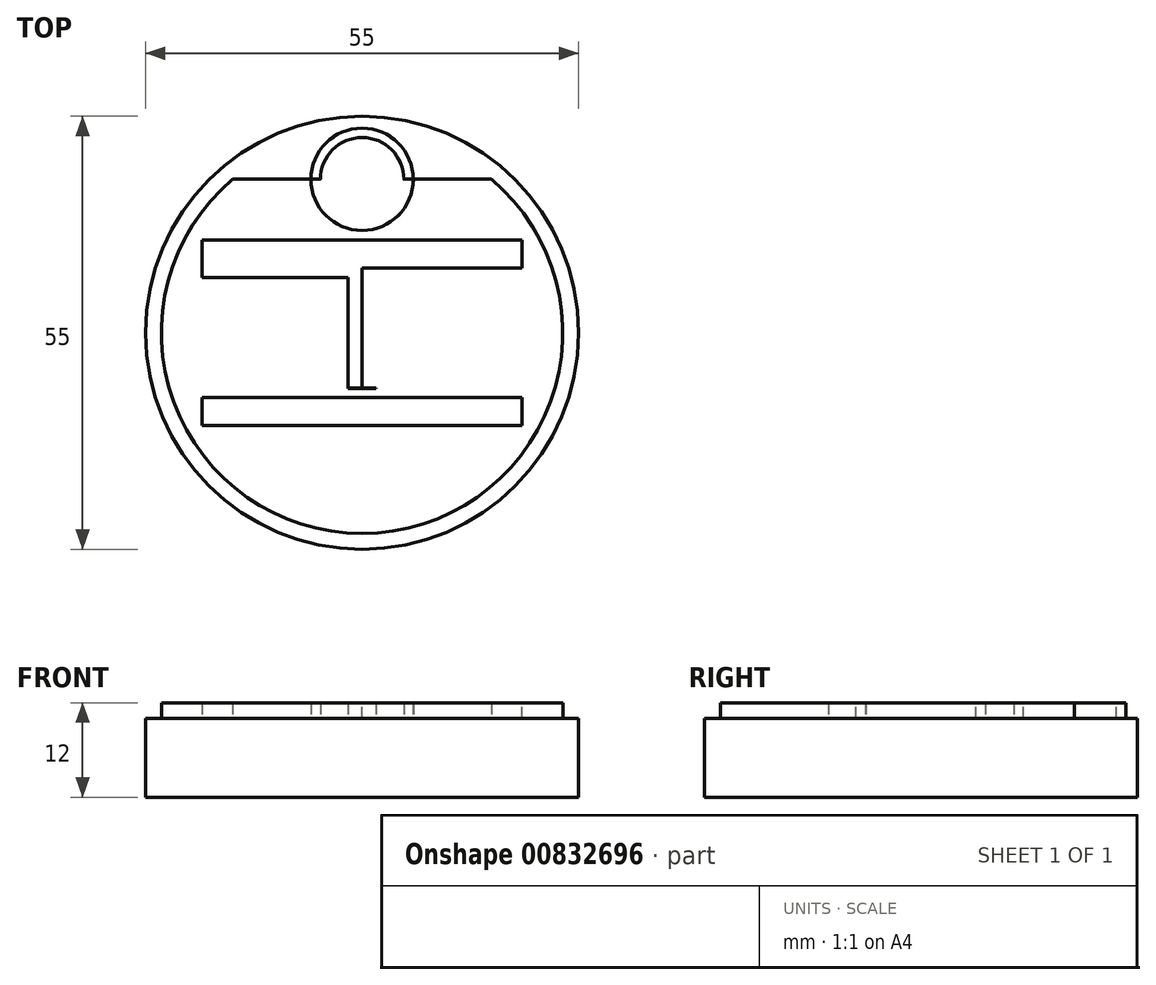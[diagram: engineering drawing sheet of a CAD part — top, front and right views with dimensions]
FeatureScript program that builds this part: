
annotation { "Feature Type Name" : "Feature", "Feature Type Description" : "" }
export const myFeature = defineFeature(function(context is Context, id is Id, definition is map)
    precondition{}
    {
        {
            var Q0;
            Q0=qCreatedBy(makeId("Top.planeOp"),FACE);
            var sketch = newSketch(context, id + "F0", { "sketchPlane" : qUnion([Q0])});
            skCircle(sketch, "E0", {"center": v(0, 0) * mm, "radius": 27.5 * mm});
            skSolve(sketch);
        }
        {
            var Q0;
            Q0=makeQuery(id+"F0.imprint","IMPRINT",FACE,{"disambiguationData":[TD([[makeQuery(id+"F0.imprint","IMPRINT",EDGE,{"derivedFrom":sQuery(id+"F0.wireOp",EDGE,"E0")}),1.0]])]});
            extrude(context, id + "F1", {"entities" : qUnion([Q0]), "depth" : 10 * mm, "offsetDistance" : 25 * mm});
        }
        {
            var Q0;
            Q0=makeQuery(id+"F1.opExtrude","CAP_FACE",FACE,{"disambiguationData":[OSD([sQuery(id+"F0.wireOp",EDGE,"E0")])],"isStart":false});
            var sketch = newSketch(context, id + "F2", { "sketchPlane" : qUnion([Q0])});
            skCircle(sketch, "E1.0", {"center": v(0, 0) * mm, "radius": 25.5 * mm});
            skLineSegment(sketch, "E2.bottom", {"start": v(-3, -7) * mm, "end": v(3, -7) * mm});
            skLineSegment(sketch, "E2.top", {"start": v(-3, 7) * mm, "end": v(3, 7) * mm});
            skLineSegment(sketch, "E2.left", {"start": v(-3, -7) * mm, "end": v(-3, 7) * mm});
            skLineSegment(sketch, "E2.right", {"start": v(3, -7) * mm, "end": v(3, 7) * mm});
            skLineSegment(sketch, "E3.0", {"start": v(-3, -10) * mm, "end": v(3, -10) * mm});
            skLineSegment(sketch, "E4.0", {"start": v(0, -7) * mm, "end": v(0, 12) * mm});
            skLineSegment(sketch, "E5.bottom", {"start": v(21.5, -7.05) * mm, "end": v(-21.5, -7.05) * mm});
            skLineSegment(sketch, "E5.top", {"start": v(21.5, -12.95) * mm, "end": v(-21.5, -12.95) * mm});
            skLineSegment(sketch, "E5.left", {"start": v(21.5, -7.05) * mm, "end": v(21.5, -12.95) * mm});
            skLineSegment(sketch, "E5.right", {"start": v(-21.5, -7.05) * mm, "end": v(-21.5, -12.95) * mm});
            skPoint(sketch, "E5.middle", {"position": v(0, -10) * mm});
            skLineSegment(sketch, "E6.0", {"start": v(-3, 10) * mm, "end": v(3, 10) * mm});
            skLineSegment(sketch, "E7.bottom", {"start": v(21.5, 13) * mm, "end": v(-21.5, 13) * mm});
            skLineSegment(sketch, "E7.top", {"start": v(21.5, 7) * mm, "end": v(-21.5, 7) * mm});
            skLineSegment(sketch, "E7.left", {"start": v(21.5, 13) * mm, "end": v(21.5, 7) * mm});
            skLineSegment(sketch, "E7.right", {"start": v(-21.5, 13) * mm, "end": v(-21.5, 7) * mm});
            skPoint(sketch, "E7.middle", {"position": v(0, 10) * mm});
            skLineSegment(sketch, "E8.0", {"start": v(21.5, 19.5) * mm, "end": v(-21.5, 19.5) * mm});
            skCircle(sketch, "E9", {"center": v(0, 19.5) * mm, "radius": 6.5 * mm});
            skCircle(sketch, "E10", {"center": v(0, 19.5) * mm, "radius": 3.5 * mm});
            skCircle(sketch, "E11.0", {"center": v(0, 19.5) * mm, "radius": 5.3 * mm});
            skLineSegment(sketch, "E12.0", {"start": v(21.5, 11.8) * mm, "end": v(-21.5, 11.8) * mm});
            skLineSegment(sketch, "E13.0", {"start": v(21.5, 8.2) * mm, "end": v(-21.5, 8.2) * mm});
            skLineSegment(sketch, "E14.0", {"start": v(-3, -6) * mm, "end": v(3, -6) * mm});
            skLineSegment(sketch, "E15.0", {"start": v(-3, 6) * mm, "end": v(3, 6) * mm});
            skLineSegment(sketch, "E16.0", {"start": v(21.5, -8.25) * mm, "end": v(-21.5, -8.25) * mm});
            skLineSegment(sketch, "E17.0", {"start": v(21.5, -11.75) * mm, "end": v(-21.5, -11.75) * mm});
            skLineSegment(sketch, "E18.0", {"start": v(1.8, -7) * mm, "end": v(1.8, 7) * mm});
            skLineSegment(sketch, "E19.0", {"start": v(-1.8, -7) * mm, "end": v(-1.8, 7) * mm});
            skLineSegment(sketch, "E20.0", {"start": v(-20.3, -7.05) * mm, "end": v(-20.3, -12.95) * mm});
            skLineSegment(sketch, "E21.0", {"start": v(20.3, -7.05) * mm, "end": v(20.3, -12.95) * mm});
            skLineSegment(sketch, "E22.0", {"start": v(20.3, 13) * mm, "end": v(20.3, 7) * mm});
            skLineSegment(sketch, "E23.0", {"start": v(-20.3, 13) * mm, "end": v(-20.3, 7) * mm});
            skLineSegment(sketch, "E24", {"start": v(-1.8, 7) * mm, "end": v(-1.8, 8.2) * mm});
            skLineSegment(sketch, "E25", {"start": v(-1.8, 8.2) * mm, "end": v(-1.8, 7) * mm});
            skLineSegment(sketch, "E26", {"start": v(1.8, 7) * mm, "end": v(1.8, 8.2) * mm});
            skLineSegment(sketch, "E27", {"start": v(1.8, 8.2) * mm, "end": v(1.8, -7) * mm});
            skLineSegment(sketch, "E28", {"start": v(1.8, -7) * mm, "end": v(1.8, -8.25) * mm});
            skLineSegment(sketch, "E29", {"start": v(1.8, -8.25) * mm, "end": v(1.8, -7) * mm});
            skLineSegment(sketch, "E30", {"start": v(-1.8, -7) * mm, "end": v(-1.8, -8.25) * mm});
            skSolve(sketch);
        }
        {
            var Q0;
            {var subQ0=sQuery(id+"F2.wireOp",EDGE,"E5.left");var subQ1=sQuery(id+"F2.wireOp",EDGE,"E5.bottom");var subQ2=makeQuery(id+"F2.imprint","INTERSECT",VERTEX,{"derivedFrom":[subQ1,subQ0]});Q0=makeQuery(id+"F2.imprint","IMPRINT",FACE,{"disambiguationData":[TD([[makeQuery(id+"F2.imprint","IMPRINT",EDGE,{"disambiguationData":[TD([[subQ2,-1.0]])],"derivedFrom":subQ1}),1.0]])]});}
            var Q1;
            {var subQ0=sQuery(id+"F2.wireOp",EDGE,"E5.right");var subQ1=sQuery(id+"F2.wireOp",EDGE,"E5.bottom");var subQ2=makeQuery(id+"F2.imprint","INTERSECT",VERTEX,{"derivedFrom":[subQ1,subQ0]});Q1=makeQuery(id+"F2.imprint","IMPRINT",FACE,{"disambiguationData":[TD([[makeQuery(id+"F2.imprint","IMPRINT",EDGE,{"disambiguationData":[TD([[subQ2,1.0]])],"derivedFrom":subQ1}),1.0]])]});}
            var Q2;
            {var subQ0=sQuery(id+"F2.wireOp",EDGE,"E21.0");var subQ1=sQuery(id+"F2.wireOp",EDGE,"E5.bottom");var subQ2=makeQuery(id+"F2.imprint","INTERSECT",VERTEX,{"derivedFrom":[subQ1,subQ0]});Q2=makeQuery(id+"F2.imprint","IMPRINT",FACE,{"disambiguationData":[TD([[makeQuery(id+"F2.imprint","IMPRINT",EDGE,{"disambiguationData":[TD([[subQ2,-1.0]])],"derivedFrom":subQ1}),1.0]])]});}
            var Q3;
            {var subQ0=sQuery(id+"F2.wireOp",EDGE,"E20.0");var subQ1=sQuery(id+"F2.wireOp",EDGE,"E5.bottom");var subQ2=makeQuery(id+"F2.imprint","INTERSECT",VERTEX,{"derivedFrom":[subQ1,subQ0]});Q3=makeQuery(id+"F2.imprint","IMPRINT",FACE,{"disambiguationData":[TD([[makeQuery(id+"F2.imprint","IMPRINT",EDGE,{"disambiguationData":[TD([[subQ2,1.0]])],"derivedFrom":subQ1}),1.0]])]});}
            var Q4;
            {var subQ0=sQuery(id+"F2.wireOp",EDGE,"E9");var subQ1=sQuery(id+"F2.wireOp",EDGE,"E1.0");var subQ2=makeQuery(id+"F2.imprint","INTERSECT",VERTEX,{"disambiguationData":[OD(0.0)],"derivedFrom":[subQ1,subQ0]});Q4=makeQuery(id+"F2.imprint","IMPRINT",FACE,{"disambiguationData":[TD([[makeQuery(id+"F2.imprint","IMPRINT",EDGE,{"disambiguationData":[TD([[subQ2,-1.0]])],"derivedFrom":subQ1}),-1.0]])]});}
            var Q5;
            {var subQ0=sQuery(id+"F2.wireOp",EDGE,"E2.right");var subQ1=sQuery(id+"F2.wireOp",EDGE,"E2.bottom");var subQ2=makeQuery(id+"F2.imprint","INTERSECT",VERTEX,{"derivedFrom":[subQ1,subQ0]});Q5=makeQuery(id+"F2.imprint","IMPRINT",FACE,{"disambiguationData":[TD([[makeQuery(id+"F2.imprint","IMPRINT",EDGE,{"disambiguationData":[TD([[subQ2,-1.0]])],"derivedFrom":subQ0}),1.0]])]});}
            var Q6;
            {var subQ0=sQuery(id+"F2.wireOp",EDGE,"E14.0");var subQ1=sQuery(id+"F2.wireOp",EDGE,"E2.right");var subQ2=makeQuery(id+"F2.imprint","INTERSECT",VERTEX,{"derivedFrom":[subQ1,subQ0]});Q6=makeQuery(id+"F2.imprint","IMPRINT",FACE,{"disambiguationData":[TD([[makeQuery(id+"F2.imprint","IMPRINT",EDGE,{"disambiguationData":[TD([[subQ2,-1.0]])],"derivedFrom":subQ1}),1.0]])]});}
            var Q7;
            {var subQ0=sQuery(id+"F2.wireOp",EDGE,"E7.top");var subQ1=sQuery(id+"F2.wireOp",EDGE,"E2.right");var subQ2=makeQuery(id+"F2.imprint","INTERSECT",VERTEX,{"derivedFrom":[subQ1,subQ0]});Q7=makeQuery(id+"F2.imprint","IMPRINT",FACE,{"disambiguationData":[TD([[makeQuery(id+"F2.imprint","IMPRINT",EDGE,{"disambiguationData":[TD([[subQ2,1.0]])],"derivedFrom":subQ1}),1.0]])]});}
            var Q8;
            {var subQ0=sQuery(id+"F2.wireOp",EDGE,"E2.left");var subQ1=sQuery(id+"F2.wireOp",EDGE,"E2.bottom");var subQ2=makeQuery(id+"F2.imprint","INTERSECT",VERTEX,{"derivedFrom":[subQ1,subQ0]});Q8=makeQuery(id+"F2.imprint","IMPRINT",FACE,{"disambiguationData":[TD([[makeQuery(id+"F2.imprint","IMPRINT",EDGE,{"disambiguationData":[TD([[subQ2,-1.0]])],"derivedFrom":subQ0}),-1.0]])]});}
            var Q9;
            {var subQ0=sQuery(id+"F2.wireOp",EDGE,"E14.0");var subQ1=sQuery(id+"F2.wireOp",EDGE,"E2.left");var subQ2=makeQuery(id+"F2.imprint","INTERSECT",VERTEX,{"derivedFrom":[subQ1,subQ0]});Q9=makeQuery(id+"F2.imprint","IMPRINT",FACE,{"disambiguationData":[TD([[makeQuery(id+"F2.imprint","IMPRINT",EDGE,{"disambiguationData":[TD([[subQ2,-1.0]])],"derivedFrom":subQ1}),-1.0]])]});}
            var Q10;
            {var subQ0=sQuery(id+"F2.wireOp",EDGE,"E7.top");var subQ1=sQuery(id+"F2.wireOp",EDGE,"E2.left");var subQ2=makeQuery(id+"F2.imprint","INTERSECT",VERTEX,{"derivedFrom":[subQ1,subQ0]});Q10=makeQuery(id+"F2.imprint","IMPRINT",FACE,{"disambiguationData":[TD([[makeQuery(id+"F2.imprint","IMPRINT",EDGE,{"disambiguationData":[TD([[subQ2,1.0]])],"derivedFrom":subQ1}),-1.0]])]});}
            var Q11;
            {var subQ3=sQuery(id+"F2.wireOp",EDGE,"E9");var subQ7=sQuery(id+"F2.wireOp",EDGE,"E1.0");var subQ8=makeQuery(id+"F2.imprint","INTERSECT",VERTEX,{"disambiguationData":[OD(0.0)],"derivedFrom":[subQ7,subQ3]});Q11=makeQuery(id+"F2.imprint","IMPRINT",FACE,{"disambiguationData":[TD([[makeQuery(id+"F2.imprint","IMPRINT",EDGE,{"disambiguationData":[TD([[subQ8,-1.0]])],"derivedFrom":subQ7}),1.0]])]});}
            var Q12;
            {var subQ0=sQuery(id+"F2.wireOp",EDGE,"E9");var subQ2=sQuery(id+"F2.wireOp",EDGE,"E8.0");var subQ3=makeQuery(id+"F2.imprint","INTERSECT",VERTEX,{"disambiguationData":[OD(0.0)],"derivedFrom":[subQ2,subQ0]});Q12=makeQuery(id+"F2.imprint","IMPRINT",FACE,{"disambiguationData":[TD([[makeQuery(id+"F2.imprint","IMPRINT",EDGE,{"disambiguationData":[TD([[subQ3,-1.0]])],"derivedFrom":subQ2}),1.0]])]});}
            var Q13;
            {var subQ0=sQuery(id+"F2.wireOp",EDGE,"E7.left");var subQ1=sQuery(id+"F2.wireOp",EDGE,"E7.bottom");var subQ2=makeQuery(id+"F2.imprint","INTERSECT",VERTEX,{"derivedFrom":[subQ1,subQ0]});Q13=makeQuery(id+"F2.imprint","IMPRINT",FACE,{"disambiguationData":[TD([[makeQuery(id+"F2.imprint","IMPRINT",EDGE,{"disambiguationData":[TD([[subQ2,-1.0]])],"derivedFrom":subQ1}),1.0]])]});}
            var Q14;
            {var subQ0=sQuery(id+"F2.wireOp",EDGE,"E7.left");var subQ1=sQuery(id+"F2.wireOp",EDGE,"E7.top");var subQ2=makeQuery(id+"F2.imprint","INTERSECT",VERTEX,{"derivedFrom":[subQ1,subQ0]});Q14=makeQuery(id+"F2.imprint","IMPRINT",FACE,{"disambiguationData":[TD([[makeQuery(id+"F2.imprint","IMPRINT",EDGE,{"disambiguationData":[TD([[subQ2,-1.0]])],"derivedFrom":subQ1}),-1.0]])]});}
            var Q15;
            {var subQ0=sQuery(id+"F2.wireOp",EDGE,"E12.0");var subQ1=sQuery(id+"F2.wireOp",EDGE,"E7.left");var subQ2=makeQuery(id+"F2.imprint","INTERSECT",VERTEX,{"derivedFrom":[subQ1,subQ0]});Q15=makeQuery(id+"F2.imprint","IMPRINT",FACE,{"disambiguationData":[TD([[makeQuery(id+"F2.imprint","IMPRINT",EDGE,{"disambiguationData":[TD([[subQ2,-1.0]])],"derivedFrom":subQ1}),-1.0]])]});}
            var Q16;
            {var subQ4=sQuery(id+"F2.wireOp",EDGE,"E22.0");var subQ5=sQuery(id+"F2.wireOp",EDGE,"E7.bottom");var subQ6=makeQuery(id+"F2.imprint","INTERSECT",VERTEX,{"derivedFrom":[subQ5,subQ4]});Q16=makeQuery(id+"F2.imprint","IMPRINT",FACE,{"disambiguationData":[TD([[makeQuery(id+"F2.imprint","IMPRINT",EDGE,{"disambiguationData":[TD([[subQ6,-1.0]])],"derivedFrom":subQ5}),1.0]])]});}
            var Q17;
            {var subQ0=sQuery(id+"F2.wireOp",EDGE,"E12.0");var subQ1=sQuery(id+"F2.wireOp",EDGE,"E7.right");var subQ2=makeQuery(id+"F2.imprint","INTERSECT",VERTEX,{"derivedFrom":[subQ1,subQ0]});Q17=makeQuery(id+"F2.imprint","IMPRINT",FACE,{"disambiguationData":[TD([[makeQuery(id+"F2.imprint","IMPRINT",EDGE,{"disambiguationData":[TD([[subQ2,-1.0]])],"derivedFrom":subQ1}),1.0]])]});}
            var Q18;
            {var subQ0=sQuery(id+"F2.wireOp",EDGE,"E7.right");var subQ1=sQuery(id+"F2.wireOp",EDGE,"E7.top");var subQ2=makeQuery(id+"F2.imprint","INTERSECT",VERTEX,{"derivedFrom":[subQ1,subQ0]});Q18=makeQuery(id+"F2.imprint","IMPRINT",FACE,{"disambiguationData":[TD([[makeQuery(id+"F2.imprint","IMPRINT",EDGE,{"disambiguationData":[TD([[subQ2,1.0]])],"derivedFrom":subQ1}),-1.0]])]});}
            var Q19;
            {var subQ0=sQuery(id+"F2.wireOp",EDGE,"E16.0");var subQ1=sQuery(id+"F2.wireOp",EDGE,"E5.right");var subQ2=makeQuery(id+"F2.imprint","INTERSECT",VERTEX,{"derivedFrom":[subQ1,subQ0]});Q19=makeQuery(id+"F2.imprint","IMPRINT",FACE,{"disambiguationData":[TD([[makeQuery(id+"F2.imprint","IMPRINT",EDGE,{"disambiguationData":[TD([[subQ2,-1.0]])],"derivedFrom":subQ1}),1.0]])]});}
            var Q20;
            {var subQ0=sQuery(id+"F2.wireOp",EDGE,"E5.right");var subQ1=sQuery(id+"F2.wireOp",EDGE,"E5.top");var subQ2=makeQuery(id+"F2.imprint","INTERSECT",VERTEX,{"derivedFrom":[subQ1,subQ0]});Q20=makeQuery(id+"F2.imprint","IMPRINT",FACE,{"disambiguationData":[TD([[makeQuery(id+"F2.imprint","IMPRINT",EDGE,{"disambiguationData":[TD([[subQ2,1.0]])],"derivedFrom":subQ1}),-1.0]])]});}
            var Q21;
            {var subQ0=sQuery(id+"F2.wireOp",EDGE,"E20.0");var subQ1=sQuery(id+"F2.wireOp",EDGE,"E5.top");var subQ2=makeQuery(id+"F2.imprint","INTERSECT",VERTEX,{"derivedFrom":[subQ1,subQ0]});Q21=makeQuery(id+"F2.imprint","IMPRINT",FACE,{"disambiguationData":[TD([[makeQuery(id+"F2.imprint","IMPRINT",EDGE,{"disambiguationData":[TD([[subQ2,1.0]])],"derivedFrom":subQ1}),-1.0]])]});}
            var Q22;
            {var subQ0=sQuery(id+"F2.wireOp",EDGE,"E16.0");var subQ1=sQuery(id+"F2.wireOp",EDGE,"E5.left");var subQ2=makeQuery(id+"F2.imprint","INTERSECT",VERTEX,{"derivedFrom":[subQ1,subQ0]});Q22=makeQuery(id+"F2.imprint","IMPRINT",FACE,{"disambiguationData":[TD([[makeQuery(id+"F2.imprint","IMPRINT",EDGE,{"disambiguationData":[TD([[subQ2,-1.0]])],"derivedFrom":subQ1}),-1.0]])]});}
            var Q23;
            {var subQ0=sQuery(id+"F2.wireOp",EDGE,"E5.left");var subQ1=sQuery(id+"F2.wireOp",EDGE,"E5.top");var subQ2=makeQuery(id+"F2.imprint","INTERSECT",VERTEX,{"derivedFrom":[subQ1,subQ0]});Q23=makeQuery(id+"F2.imprint","IMPRINT",FACE,{"disambiguationData":[TD([[makeQuery(id+"F2.imprint","IMPRINT",EDGE,{"disambiguationData":[TD([[subQ2,-1.0]])],"derivedFrom":subQ1}),-1.0]])]});}
            var Q24;
            {var subQ0=sQuery(id+"F2.wireOp",EDGE,"E7.right");var subQ1=sQuery(id+"F2.wireOp",EDGE,"E7.bottom");var subQ2=makeQuery(id+"F2.imprint","INTERSECT",VERTEX,{"derivedFrom":[subQ1,subQ0]});Q24=makeQuery(id+"F2.imprint","IMPRINT",FACE,{"disambiguationData":[TD([[makeQuery(id+"F2.imprint","IMPRINT",EDGE,{"disambiguationData":[TD([[subQ2,1.0]])],"derivedFrom":subQ1}),1.0]])]});}
            var Q25;
            {var subQ6=sQuery(id+"F2.wireOp",EDGE,"E25");Q25=makeQuery(id+"F2.imprint","IMPRINT",FACE,{"disambiguationData":[TD([[makeQuery(id+"F2.imprint","IMPRINT",EDGE,{"derivedFrom":subQ6}),-1.0]])]});}
            var Q26;
            {var subQ1=sQuery(id+"F2.wireOp",EDGE,"E7.top");var subQ7=makeQuery(id+"F2.imprint","INTERSECT",VERTEX,{"derivedFrom":[sQuery(id+"F2.wireOp",EDGE,"E2.right"),subQ1]});Q26=makeQuery(id+"F2.imprint","IMPRINT",FACE,{"disambiguationData":[TD([[makeQuery(id+"F2.imprint","IMPRINT",EDGE,{"disambiguationData":[TD([[subQ7,1.0]])],"derivedFrom":subQ1}),-1.0]])]});}
            var Q27;
            {var subQ0=sQuery(id+"F2.wireOp",EDGE,"E7.top");var subQ1=sQuery(id+"F2.wireOp",EDGE,"E4.0");var subQ2=makeQuery(id+"F2.imprint","INTERSECT",VERTEX,{"derivedFrom":[subQ1,subQ0]});Q27=makeQuery(id+"F2.imprint","IMPRINT",FACE,{"disambiguationData":[TD([[makeQuery(id+"F2.imprint","IMPRINT",EDGE,{"disambiguationData":[TD([[subQ2,-1.0]])],"derivedFrom":subQ1}),-1.0]])]});}
            var Q28;
            {var subQ5=sQuery(id+"F2.wireOp",EDGE,"E25");Q28=makeQuery(id+"F2.imprint","IMPRINT",FACE,{"disambiguationData":[TD([[makeQuery(id+"F2.imprint","IMPRINT",EDGE,{"derivedFrom":subQ5}),1.0]])]});}
            var Q29;
            {var subQ0=sQuery(id+"F2.wireOp",EDGE,"E29");var subQ1=sQuery(id+"F2.wireOp",EDGE,"E5.bottom");var subQ2=makeQuery(id+"F2.imprint","INTERSECT",VERTEX,{"derivedFrom":[subQ1,subQ0]});Q29=makeQuery(id+"F2.imprint","IMPRINT",FACE,{"disambiguationData":[TD([[makeQuery(id+"F2.imprint","IMPRINT",EDGE,{"disambiguationData":[TD([[subQ2,-1.0]])],"derivedFrom":subQ1}),1.0]])]});}
            extrude(context, id + "F3", {"entities" : qUnion([Q0, Q1, Q2, Q3, Q4, Q5, Q6, Q7, Q8, Q9, Q10, Q11, Q12, Q13, Q14, Q15, Q16, Q17, Q18, Q19, Q20, Q21, Q22, Q23, Q24, Q25, Q26, Q27, Q28, Q29]), "operationType" : NewBodyOperationType.ADD, "depth" : 2 * mm, "offsetDistance" : 25 * mm, "hasDraft" : true, "draftAngle" : .1 * degree, "draftPullDirection" : true});
        }
    });
